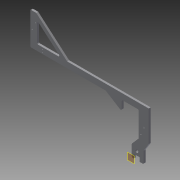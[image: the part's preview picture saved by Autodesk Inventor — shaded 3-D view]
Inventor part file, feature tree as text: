
AUTODESK INVENTOR PART (.ipt)
format: ipt  version: 2013 (Build 170138000, 138)  size: 224,768 bytes
history: native  units: in
note: dims shown in document units (in); Inventor stores cm internally (conversion verified against a paired STEP export)
features: extrude x5, sketch x4, fillet x3, plane x2
ambient origin geometry x8: Origin, YZ Plane, XZ Plane, XY Plane, X Axis, Y Axis, Z Axis, Center Point
feature tree (14):
  plane  "Work Plane4"
  plane  "Work Plane3"
  extrude  "Extrusion9"  Depth=1.25in
  extrude  "Extrusion10"  Depth=2.0in
  extrude  "Extrusion11"  Depth=0.75in
  fillet  "Fillet8"  Radius=1.5in
  fillet  "Fillet9"  [1 undecoded]
  extrude  "Extrusion12"  Depth=0.875in
  extrude  "Extrusion13"  TaperAngle=0.0deg  [1 undecoded]
  fillet  "Fillet11"  Radius=6.625in
  sketch  "Sketch8"  dims[d0=0.25in d1=0.5in d2=0.75in d3=0.25in d4=0.5in d5=0.3765in d6=0.5in d8=14.875in d17=4.0833in d19=0.375in d25=1.25in]
  sketch  "Sketch9"  dims[d26=0.125in d27=2.0in]
  sketch  "Sketch10"  dims[d28=1.0in d29=1.0in d30=0.75in d63=1.5in d68=0.0in]
  sketch  "Sketch11"  dims[d69=2.15in d71=0.875in d72=0.0in d73=6.625in d74=3.125in d76=9.475in d87=0.25in d88=1.5in d89=1.0in d91=1.0in d93=0.2797in d94=0.5in d97=0.2797in d98=10.5406in d99=0.25in d100=0.0in d101=0.15in d102=0.15in d103=0.6355in d104=1.113in d105=0.2375in d106=2.019in d107=0.25in d108=0.0in d109=0.125in d110=0.125in d111=1.5in d112=1.5in d113=0.25in d114=0.25in d115=0.125in d116=0.125in d117=1.5in d118=1.5in d119=0.1875in d121=0.25in d122=0.0in d123=0.125in d124=0.3125in d125=0.125in d126=1.5in d127=0.15in d128=0.15in d129=0.398in d130=0.906in d131=0.237in d132=0.125in d133=0.25in d134=0.0in d135=1.0in d136=1.0in d139=0.25in d140=1.0in d141=0.0in d143=0.85in d144=0.25in d145=0.125in]
note: 2 required parameter values undecoded (feature->parameter linkage not recoverable at this tier; creation-order binding heuristic only, values carry confidence <= 0.55)
